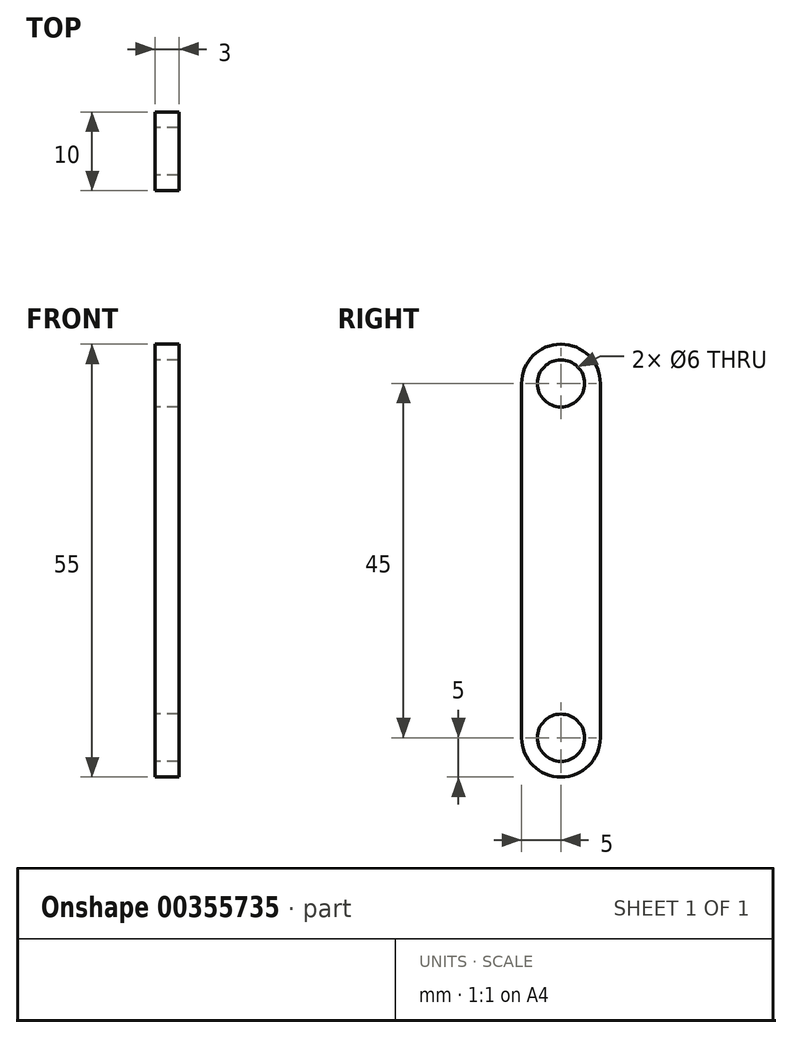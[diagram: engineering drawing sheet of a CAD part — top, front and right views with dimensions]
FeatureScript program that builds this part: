
annotation { "Feature Type Name" : "Feature", "Feature Type Description" : "" }
export const myFeature = defineFeature(function(context is Context, id is Id, definition is map)
    precondition{}
    {
        {
            var Q0;
            Q0=qCreatedBy(makeId("Right.planeOp"),FACE);
            var sketch = newSketch(context, id + "F0", { "sketchPlane" : qUnion([Q0])});
            skLineSegment(sketch, "E0", {"start": v(-5, 0) * mm, "end": v(-5, -45) * mm});
            skLineSegment(sketch, "E1", {"start": v(5, 0) * mm, "end": v(5, -45) * mm});
            skLineSegment(sketch, "E2", {"start": v(-30.93, 0) * mm, "end": v(48.16, 0) * mm, "construction": true});
            skLineSegment(sketch, "E3", {"start": v(-31.4, -45) * mm, "end": v(48.64, -45) * mm, "construction": true});
            skCircle(sketch, "E4", {"center": v(0, 0) * mm, "radius": 3 * mm});
            skCircle(sketch, "E5", {"center": v(0, -45) * mm, "radius": 3 * mm});
            skArc(sketch, "E6", {"start": v(-5, -45) * mm, "mid": v(0, -50) * mm, "end": v(5, -45) * mm});
            skArc(sketch, "E7", {"start": v(5, 0) * mm, "mid": v(0, 5) * mm, "end": v(-5, 0) * mm});
            skSolve(sketch);
        }
        {
            var Q0;
            Q0=makeQuery(id+"F0.imprint","IMPRINT",FACE,{"disambiguationData":[TD([[makeQuery(id+"F0.imprint","IMPRINT",EDGE,{"derivedFrom":sQuery(id+"F0.wireOp",EDGE,"E0")}),1.0]])]});
            extrude(context, id + "F1", {"entities" : qUnion([Q0]), "depth" : 3 * mm});
        }
    });
